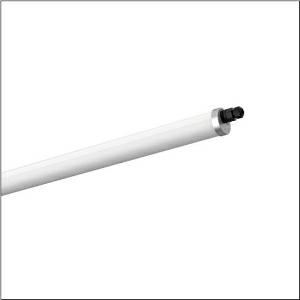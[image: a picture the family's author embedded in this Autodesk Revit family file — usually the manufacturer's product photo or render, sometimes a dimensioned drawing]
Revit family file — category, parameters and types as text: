
# Revit family: monsun_r__31_tube_51ft107n4a0a_c9dd
name_source: partatom
category: Lighting Fixtures
units: mm (PartAtom-declared; Revit-internal decimal feet)

## family parameters
Cut with Voids When Loaded = No
Host = Face
Light Source = No
Part Type = Normal
Room Calculation Point = No
Round Connector Dimension = Use Diameter
Shared = No

## types (1)
- Monsun® 31 Tube (1 x LED, 10000 lm, 58 W, 4000K)
    Apparent Load = 58 VA
    CIE Flux Codes = 42 71 90 91 100
    Color Rendering = 80
    Color Temperature = 4000K
    Default Elevation = 1800 mm
    Description = Monsun® 31 Tube, tubular luminaire, primary optical cover: diffuser, of PMMA, light emission: direct distribution, primary light characteristic: symmetric, installation type: suspended mounting, surface-mounted, LED, rated luminous flux: 10.000lm, luminous efficacy: 160lm/W, light colour: 840, colour temperature: 4000K, control gear: ON/OFF, with with 1 terminal, 3-pole, max. 2.5mm², through-wiring: 3x 1.5mm², mains connection: 220..240V, AC, 50/60Hz, rated input power: 58W, housing, cylindrical, of PMMA, semi-transparent, matt white, with luminaire and ceiling fastening, V4A, mounting with brackets of stainless steel, length: 1.560mm, diameter: 75mm, end cap, of stainless steel (V4A), protection rating (complete): IP67/IP69K, insulation class (complete): insulation class I (protective earthing), certification: CE, UKCA, impact resistance: IK07, permissible operating ambient temperature: -20..+40°C, corresponds to IFS (International Featured Standards) requirements for safety and quality in the food industry, usage in unprotected outdoor areas possible with horizontal mounting, contact your sales advisor before using the luminaires in applications with unclear chemical exposure, large temperature fluctuations or condensation-forming humidity, packaging unit: 1 piece
    Height = 83 mm
    Lamp = 1 x LED
    Lamp Light Flux = 10000 lm
    Lamp Power = 58 W
    Lamp count = 1
    Length = 1560 mm
    Luminous efficacy = 172 lm/W
    Manufacturer = Siteco
    ModVariant = No
    Model = 51FT107N4A0A
    Mounting Place = Ceiling
    Mounting Type = Pendant
    Number of Poles = 1
    OnlyDefault = Yes
    Power Factor = 1
    Product Name = Monsun® 31 Tube
    Product group = tubular luminaire
    ProductGroupID = 906
    Protection Class = Protection class I
    RLX_Detail_Level = 1
    RLX_Emergency_Light_Flux = 0 lm
    RLX_Emergency_Type = 0
    RLX_Emergency_Type_DB = No
    RlxData = <blob elided: 25421 chars, md5=729f6085>
    Socket = socket
    Standby Power = 0 W
    System Light Flux = 10000 lm
    System Power = 58 W
    Type Comments = Product without accessories
    Type Image = l_1228461.jpg
    URL = http://relux.com
    VarID = ---
    Voltage = 0 V
    Weight = 0.00 kg
    Width = 75 mm

## geometry (parser evidence)
native form markers: Blend x4, Sweep x13
no freeform markers — native parametric forms only
